# Revit family: Electrical_Controls_Conspec_CX-Series-Fixed-Gas-Detector
name_source: partatom
category: Electrical Fixtures
units: mm (PartAtom-declared; Revit-internal decimal feet)

## family parameters
Classification Number = 23.85.30.21
Cut with Voids When Loaded = No
Host = Face
Maintain Annotation Orientation = No
Part Type = Normal
Room Calculation Point = No
Round Connector Dimension = Use Diameter
Shared = No

## types (13) — shared parameters
Apparent Load = 0 VA
Assembly Code = D5030
Cable Requirements = 3-Conductor 18 AWG Suggested
Current Consumption = 50 mA
Date Updated = 2023/10/17
Depth = 5.09 "
Description = CX Series Fixed Gas Detector
Display = 2 line, 8 character Alphanumeric LCD
Enclosure Rating and Finish = Explosion Proof (FM, CSA Listed), Corrosion-Resistant, Polyester Powder Coated
Frequency = 0 Hz
Height = 7.5 "
Keynote = 16000
Manufacturer = CONSPEC Controls
Models = 2 (Calibration & Normal)
Number of Poles = 3
Operating Humidity = 10% to 95% RH Non-Condesing
Operating Temperature = -4°F to +140°F
Output Signal = Linear 4-20mA
Power Factor = 0.8
Product Material = Conspec - Metal - Steel - Powder Coated - Blue
Product data url = https://bimobject.com
Sensory Types = Electrochemical, Catalytic Bead, Infrared, Photo-Ionization, Thermal Conductivity
URL = https://www.conspec-controls.com
Version = 1
Voltage = 24 V
Voltage Range = 12V - 24V DC
Weight = 3.00 lbf
Width = 5.71 "
zero-valued in all types: Default Elevation

## per-type parameters (varying)
| type | Gas Detecting | Model |
| CX – Sulfur Dioxide | Sulfur Dioxide | CX13 |
| CX – Ozone | Ozone | CX12 |
| CX – Oxygen | Oxygen | CX11 |
| CX – Nitrogen Dioxide | Nitrogen Dioxide | CX10 |
| CX – Nitric Oxide | Nitric Oxide | CX09 |
| CX – Hydrogen Sulfide | Hydrogen Sulfide | CX08 |
| CX – Hydrogen Chloride | Hydrogen Chloride | CX07 |
| CX – Hydrogen | Hydrogen | CX06 |
| CX – Combustibles | Combustibles | CX05 |
| CX – Chlorine | Chlorine | CX04 |
| CX – Carbon Monoxide | Carbon Monoxide | CX03 |
| CX – Carbon Dioxide | Carbon Dioxide | CX02 |
| CX – Ammonia | Ammonia | CX01 |

## geometry (parser evidence)
native form markers: Sweep x3
no freeform markers — native parametric forms only
